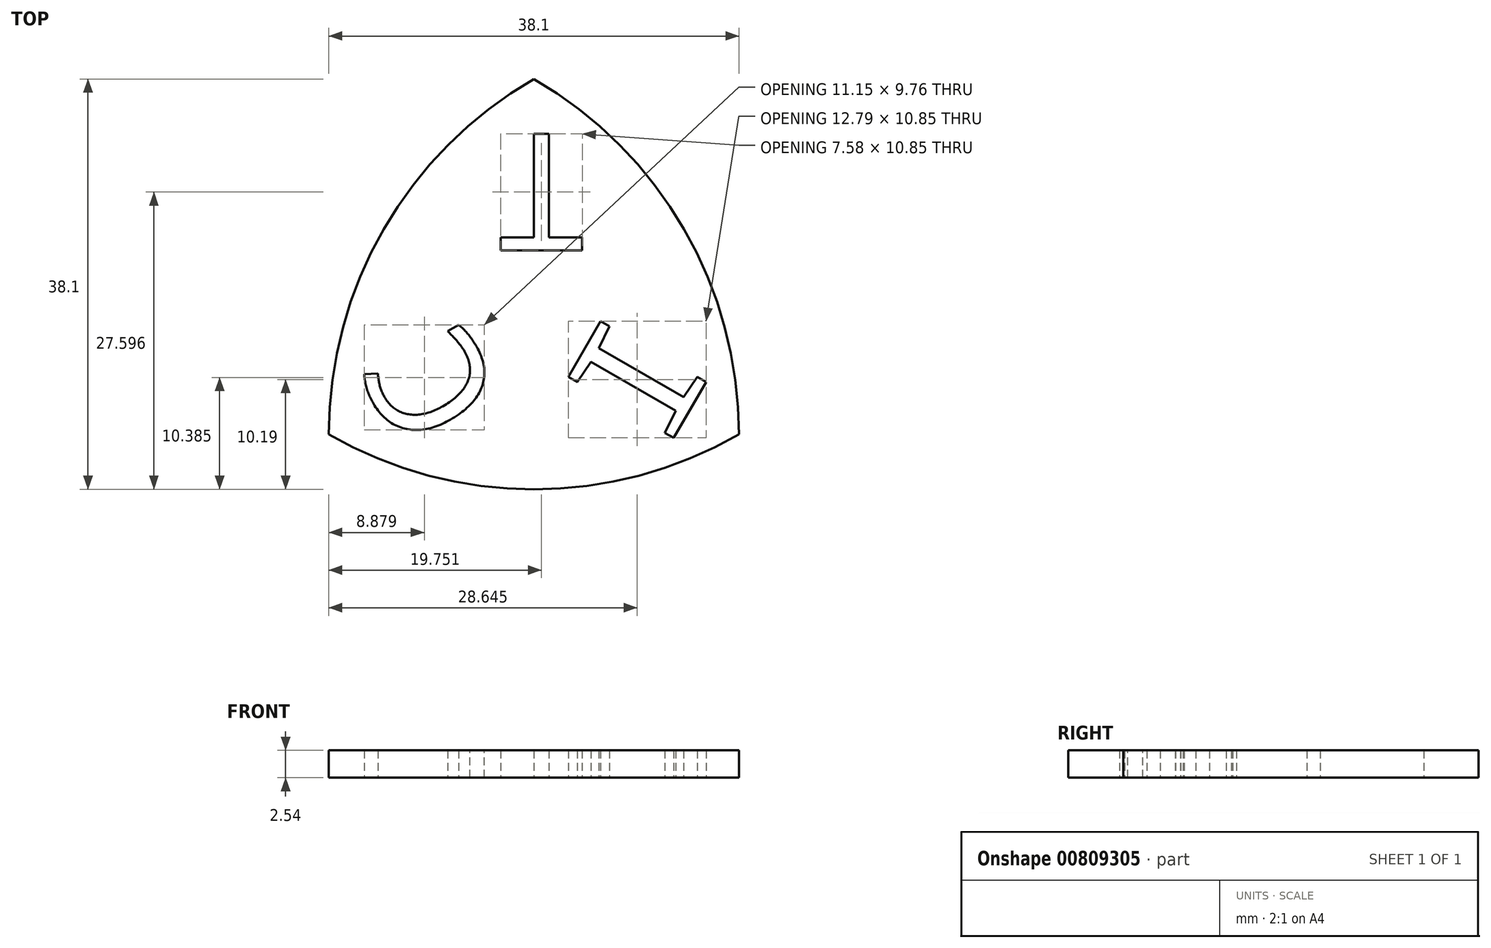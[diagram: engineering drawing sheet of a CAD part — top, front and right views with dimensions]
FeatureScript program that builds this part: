
annotation { "Feature Type Name" : "Feature", "Feature Type Description" : "" }
export const myFeature = defineFeature(function(context is Context, id is Id, definition is map)
    precondition{}
    {
        {
            var Q0;
            Q0=qCreatedBy(makeId("Top.planeOp"),FACE);
            var sketch = newSketch(context, id + "F0", { "sketchPlane" : qUnion([Q0])});
            skCircle(sketch, "E0", {"center": v(0, 0) * mm, "radius": 38.1 * mm});
            skSolve(sketch);
        }
        {
            var Q0;
            Q0=qCreatedBy(makeId("Top.planeOp"),FACE);
            var sketch = newSketch(context, id + "F1", { "sketchPlane" : qUnion([Q0])});
            skCircle(sketch, "E1", {"center": v(-38.1, 0) * mm, "radius": 38.1 * mm});
            skSolve(sketch);
        }
        {
            var Q0;
            Q0=qCreatedBy(makeId("Top.planeOp"),FACE);
            var sketch = newSketch(context, id + "F2", { "sketchPlane" : qUnion([Q0])});
            skCircle(sketch, "E2", {"center": v(-19.05, 33) * mm, "radius": 38.1 * mm});
            skSolve(sketch);
        }
        {
            var Q0;
            Q0=makeQuery(id+"F0.imprint","IMPRINT",FACE,{"disambiguationData":[TD([[makeQuery(id+"F0.imprint","IMPRINT",EDGE,{"derivedFrom":sQuery(id+"F0.wireOp",EDGE,"E0")}),1.0]])]});
            extrude(context, id + "F3", {"entities" : qUnion([Q0]), "depth" : 2.54 * mm, "offsetDistance" : 25.4 * mm});
        }
        {
            var Q0;
            Q0=makeQuery(id+"F1.imprint","IMPRINT",FACE,{"disambiguationData":[TD([[makeQuery(id+"F1.imprint","IMPRINT",EDGE,{"derivedFrom":sQuery(id+"F1.wireOp",EDGE,"E1")}),1.0]])]});
            extrude(context, id + "F4", {"entities" : qUnion([Q0]), "depth" : 2.54 * mm, "offsetDistance" : 25.4 * mm});
        }
        {
            var Q0;
            Q0=makeQuery(id+"F2.imprint","IMPRINT",FACE,{"disambiguationData":[TD([[makeQuery(id+"F2.imprint","IMPRINT",EDGE,{"derivedFrom":sQuery(id+"F2.wireOp",EDGE,"E2")}),1.0]])]});
            extrude(context, id + "F5", {"entities" : qUnion([Q0]), "depth" : 2.54 * mm, "offsetDistance" : 25.4 * mm});
        }
        {
            var Q0;
            Q0=makeQuery(id+"F4.opExtrude","SWEPT_BODY",BODY,{"disambiguationData":[OSD([sQuery(id+"F1.wireOp",EDGE,"E1")])]});
            var Q1;
            Q1=makeQuery(id+"F3.opExtrude","SWEPT_BODY",BODY,{"disambiguationData":[OSD([sQuery(id+"F0.wireOp",EDGE,"E0")])]});
            var Q2;
            Q2=makeQuery(id+"F5.opExtrude","SWEPT_BODY",BODY,{"disambiguationData":[OSD([sQuery(id+"F2.wireOp",EDGE,"E2")])]});
            booleanBodies(context, id + "F6", {"operationType" : BooleanOperationType.INTERSECTION, "tools" : qUnion([Q0, Q1, Q2])});
        }
        {
            var Q0;
            Q0=qCreatedBy(makeId("Top.planeOp"),FACE);
            var sketch = newSketch(context, id + "F7", { "sketchPlane" : qUnion([Q0])});
            skText(sketch, "E3", { "text": "C", "fontName": "DroidSansMono.ttf"});
            skText(sketch, "E4", { "text": "I", "fontName": "DroidSansMono.ttf"});
            skText(sketch, "E5", { "text": "T", "fontName": "DroidSansMono.ttf"});
            const initialGuessF7  = {"E3": [-0.0217, 0.00322, -0.5, 0.86603, 0.01073], "E4": [-0.00693, -0.00184, 0.5, 0.86603, 0.0114], "E5": [-0.0138, 0.02792, -1, 0, 0.01094]};
            skSetInitialGuess(sketch, initialGuessF7);
            skSolve(sketch);
        }
        {
            var Q0;
            Q0 = qSketchRegion(id + "F7", true);
            extrude(context, id + "F8", {"entities" : qUnion([Q0]), "operationType" : NewBodyOperationType.REMOVE, "depth" : 25.4 * mm, "offsetDistance" : 25.4 * mm});
        }
    });
